# Revit family: Trane_TVR_Indoor_High static pressure_4TVA0068(85,95)EF000AA(2nd DC)
name_source: partatom
category: Equipamento mecânico
units: mm (PartAtom-declared; Revit-internal decimal feet)

## family parameters
Com base no plano de trabalho = Não
Compartilhado = Não
Corte com vazios quando carregada = Não
Cota do conector redondo = Utilizar diâmetro
Número OmniClass = 23.75.00.00
Ponto de cálculo do ambiente = Não
Sempre na vertical = Sim
Tipo de parte = Normal
Título OmniClass = Climate Control (HVAC)

## types (3) — shared parameters
Air  Flow = 4330/4230/4130/4030/3930/3830/3730 m3/h
Condensation = air
Depth = 931  [stored 3.05446 ft]
Descrição = High efficiency air cooled
Fabricante = Trane
Gas = R410a
Gas pipe = 22.2  [stored 0.0728346 ft]
Height = 515  [stored 1.68963 ft]
Installation = Indoor installation
Liquid pipe = 12.7  [stored 0.0416667 ft]
Maximum Fuse Amps = 15 A
Minimum Circuit Amps = 5 A
Net Weight = 130.00 kg
Power supply = 220-240V ~50/60Hz
Series = Ultra
URL = https://www.trane.com
Width = 1454  [stored 4.77034 ft]
clearance access behind = 600  [stored 1.9685 ft]
clearance access front = 500  [stored 1.64042 ft]
clearance access left = 600  [stored 1.9685 ft]
clearance access right = 600  [stored 1.9685 ft]

## per-type parameters (varying)
| type | Cooling Capacity | Cooling Power Input | Heating Capacity | Heating Power Input |
| 4TVA0068EF000AA | 22.50 kW | 990.000 W | 20.00 kW | 990.000 W |
| 4TVA0085EF000AA | 25.00 kW | 1200.000 W | 26.00 kW | 1200.000 W |
| 4TVA0095EF000AA | 28.00 kW | 850.000 W | 31.50 kW | 850.000 W |

note: column(s) folded — value = type name in every type: Modelo

note: [stored X ft] marks values corroborated as IEEE doubles in the binary element streams (Revit-internal decimal feet)

## geometry (parser evidence)
native form markers: Blend x4, Sweep x10
no freeform markers — native parametric forms only
